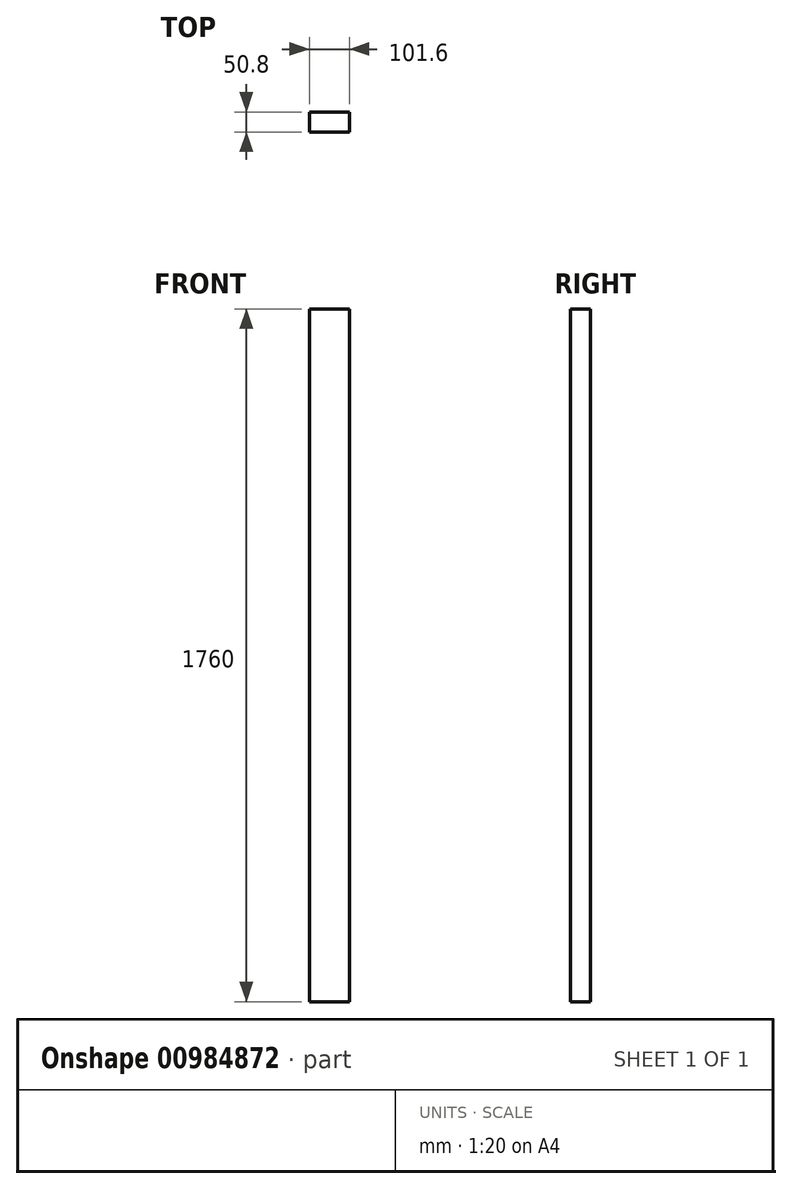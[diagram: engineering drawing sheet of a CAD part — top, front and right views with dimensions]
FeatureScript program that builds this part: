
annotation { "Feature Type Name" : "Feature", "Feature Type Description" : "" }
export const myFeature = defineFeature(function(context is Context, id is Id, definition is map)
    precondition{}
    {
        {
            var Q0;
            Q0=qCreatedBy(makeId("Front.planeOp"),FACE);
            var sketch = newSketch(context, id + "F0", { "sketchPlane" : qUnion([Q0])});
            skLineSegment(sketch, "E0.bottom", {"start": v(0, 0) * mm, "end": v(101.6, 0) * mm});
            skLineSegment(sketch, "E0.top", {"start": v(0, 1760) * mm, "end": v(101.6, 1760) * mm});
            skLineSegment(sketch, "E0.left", {"start": v(0, 0) * mm, "end": v(0, 1760) * mm});
            skLineSegment(sketch, "E0.right", {"start": v(101.6, 0) * mm, "end": v(101.6, 1760) * mm});
            skSolve(sketch);
        }
        {
            var Q0;
            Q0=makeQuery(id+"F0.imprint","IMPRINT",FACE,{"disambiguationData":[TD([[makeQuery(id+"F0.imprint","IMPRINT",EDGE,{"derivedFrom":sQuery(id+"F0.wireOp",EDGE,"E0.bottom")}),1.0]])]});
            extrude(context, id + "F1", {"entities" : qUnion([Q0]), "oppositeDirection" : true, "depth" : 50.8 * mm, "offsetDistance" : 25 * mm});
        }
    });
